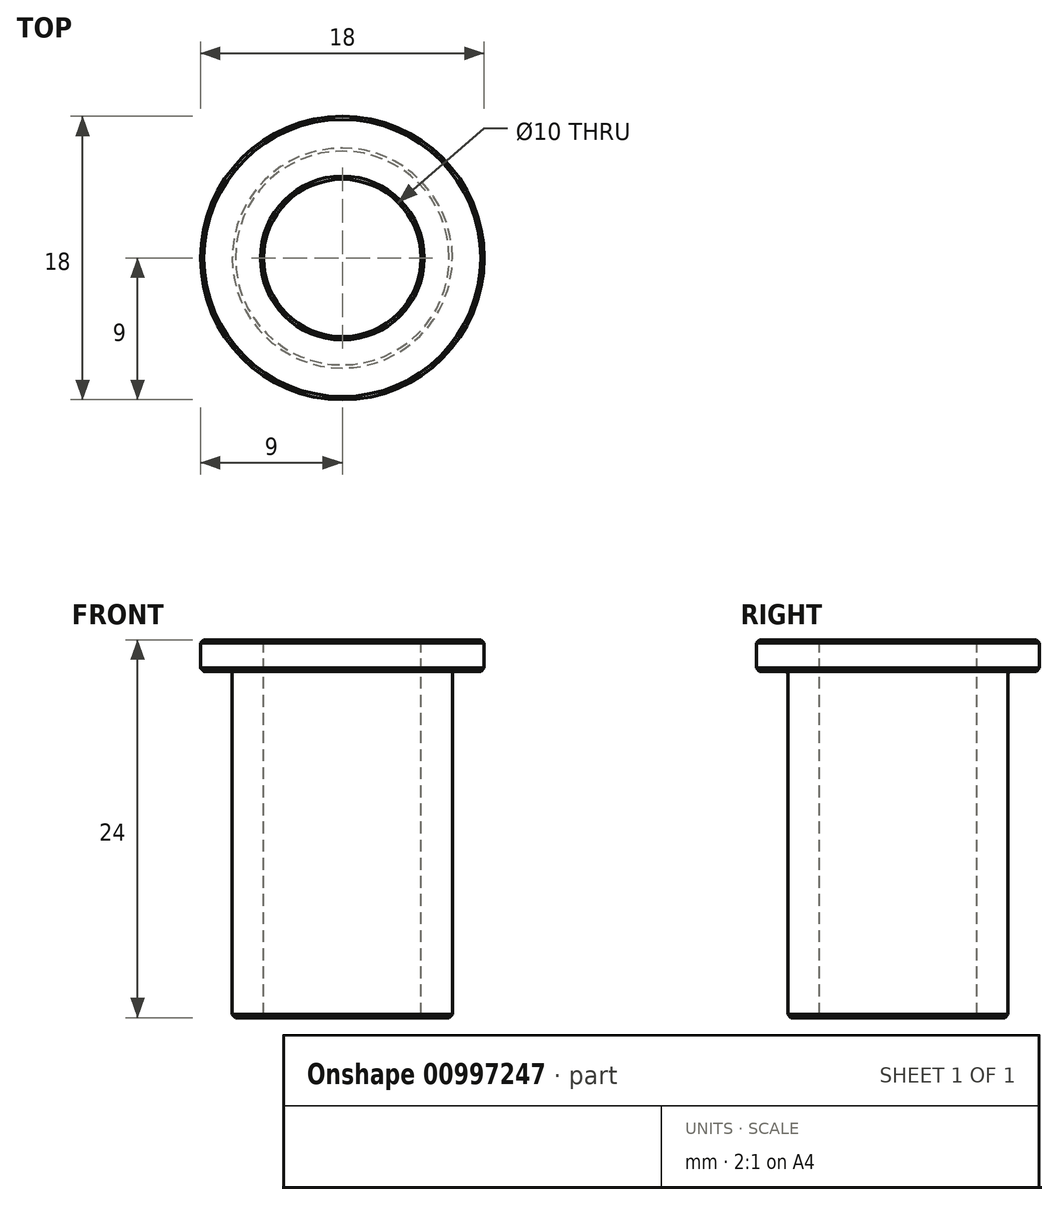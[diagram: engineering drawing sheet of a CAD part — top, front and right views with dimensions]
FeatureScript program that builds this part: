
annotation { "Feature Type Name" : "Feature", "Feature Type Description" : "" }
export const myFeature = defineFeature(function(context is Context, id is Id, definition is map)
    precondition{}
    {
        {
            var Q0;
            Q0=qCreatedBy(makeId("Front.planeOp"),FACE);
            var sketch = newSketch(context, id + "F0", { "sketchPlane" : qUnion([Q0])});
            skLineSegment(sketch, "E0", {"start": v(0, 12) * mm, "end": v(-9, 12) * mm});
            skLineSegment(sketch, "E1", {"start": v(-9, 12) * mm, "end": v(-9, 10) * mm});
            skLineSegment(sketch, "E2", {"start": v(-9, 10) * mm, "end": v(-7, 10) * mm});
            skLineSegment(sketch, "E3", {"start": v(-7, 10) * mm, "end": v(-6.99, -12) * mm});
            skLineSegment(sketch, "E4", {"start": v(-6.99, -12) * mm, "end": v(0, -12) * mm});
            skLineSegment(sketch, "E5", {"start": v(0, -12) * mm, "end": v(0, 12) * mm});
            skLineSegment(sketch, "E6", {"start": v(0, 26.43) * mm, "end": v(0, -27.72) * mm, "construction": true});
            skSolve(sketch);
        }
        {
            var Q0;
            Q0 = qSketchRegion(id + "F0", true);
            var Q1;
            Q1=sQuery(id+"F0.wireOp",EDGE,"E6");
            revolve(context, id + "F1", {"surfaceOperationType" : NewSurfaceOperationType.NEW, "entities" : qUnion([Q0]), "axis" : qUnion([Q1]), "revolveType" : RevolveType.FULL});
        }
        {
            var Q0;
            Q0=qCreatedBy(makeId("Top.planeOp"),FACE);
            var sketch = newSketch(context, id + "F2", { "sketchPlane" : qUnion([Q0])});
            skCircle(sketch, "E7", {"center": v(0, 0) * mm, "radius": 5 * mm});
            skSolve(sketch);
        }
        {
            var Q0;
            Q0 = qSketchRegion(id + "F2", true);
            extrude(context, id + "F3", {"entities" : qUnion([Q0]), "operationType" : NewBodyOperationType.REMOVE, "endBound" : BoundingType.THROUGH_ALL, "oppositeDirection" : true, "depth" : 25 * mm, "offsetDistance" : 25 * mm, "hasSecondDirection" : true, "secondDirectionOppositeDirection" : false, "secondDirectionDepth" : 25 * mm});
        }
        {
            var Q0;
            Q0=makeQuery(id+"F3.boolean.opBoolean","INTERSECT",EDGE,{"derivedFrom":[makeQuery(id+"F1.opRevolve","SWEPT_FACE",FACE,{"disambiguationData":[OSD([sQuery(id+"F0.wireOp",EDGE,"E4")])]}),makeQuery(id+"F3.opExtrude","SWEPT_FACE",FACE,{"disambiguationData":[OSD([sQuery(id+"F2.wireOp",EDGE,"E7")])]})]});
            var Q1;
            Q1=makeQuery(id+"F1.opRevolve","SWEPT_EDGE",EDGE,{"disambiguationData":[OSD([sQuery(id+"F0.wireOp",EDGE,"E3"),sQuery(id+"F0.wireOp",EDGE,"E4")])]});
            var Q2;
            Q2=makeQuery(id+"F1.opRevolve","SWEPT_EDGE",EDGE,{"disambiguationData":[OSD([sQuery(id+"F0.wireOp",EDGE,"E1"),sQuery(id+"F0.wireOp",EDGE,"E2")])]});
            var Q3;
            Q3=makeQuery(id+"F1.opRevolve","SWEPT_EDGE",EDGE,{"disambiguationData":[OSD([sQuery(id+"F0.wireOp",EDGE,"E0"),sQuery(id+"F0.wireOp",EDGE,"E1")])]});
            var Q4;
            Q4=makeQuery(id+"F3.boolean.opBoolean","INTERSECT",EDGE,{"derivedFrom":[makeQuery(id+"F1.opRevolve","SWEPT_FACE",FACE,{"disambiguationData":[OSD([sQuery(id+"F0.wireOp",EDGE,"E0")])]}),makeQuery(id+"F3.opExtrude","SWEPT_FACE",FACE,{"disambiguationData":[OSD([sQuery(id+"F2.wireOp",EDGE,"E7")])]})]});
            chamfer(context, id + "F4", {"entities" : qUnion([Q0, Q1, Q2, Q3, Q4]), "width" : 0.2 * mm, "tangentPropagation" : true});
        }
        {
            var Q0;
            Q0=makeQuery(id+"F1.opRevolve","SWEPT_EDGE",EDGE,{"disambiguationData":[OSD([sQuery(id+"F0.wireOp",EDGE,"E2"),sQuery(id+"F0.wireOp",EDGE,"E3")])]});
            fillet(context, id + "F5", {"entities" : qUnion([Q0]), "radius" : 0.2 * mm, "tangentPropagation" : true, "allowEdgeOverflow" : false});
        }
    });
